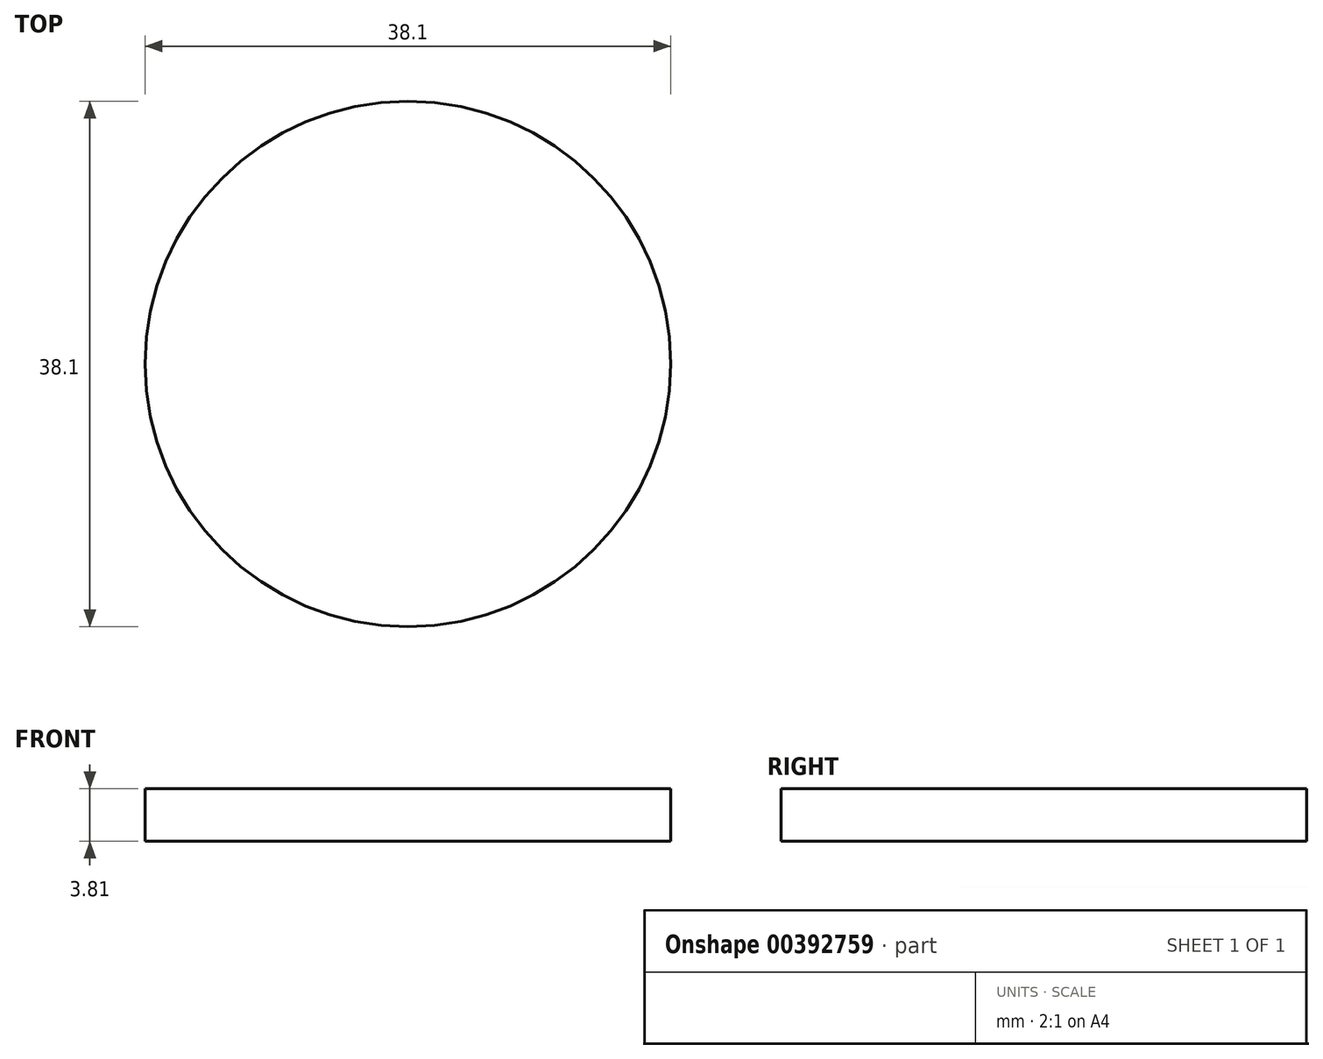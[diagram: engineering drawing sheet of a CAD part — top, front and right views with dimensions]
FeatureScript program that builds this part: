
annotation { "Feature Type Name" : "Feature", "Feature Type Description" : "" }
export const myFeature = defineFeature(function(context is Context, id is Id, definition is map)
    precondition{}
    {
        {
            var Q0;
            Q0=qCreatedBy(makeId("Top.planeOp"),FACE);
            var sketch = newSketch(context, id + "F0", { "sketchPlane" : qUnion([Q0])});
            skCircle(sketch, "E0", {"center": v(0, 0) * mm, "radius": 19.05 * mm});
            skSolve(sketch);
        }
        {
            var Q0;
            Q0=makeQuery(id+"F0.imprint","IMPRINT",FACE,{"disambiguationData":[TD([[makeQuery(id+"F0.imprint","IMPRINT",EDGE,{"derivedFrom":sQuery(id+"F0.wireOp",EDGE,"E0")}),1.0]])]});
            extrude(context, id + "F1", {"entities" : qUnion([Q0]), "depth" : 3.8 * mm});
        }
    });
